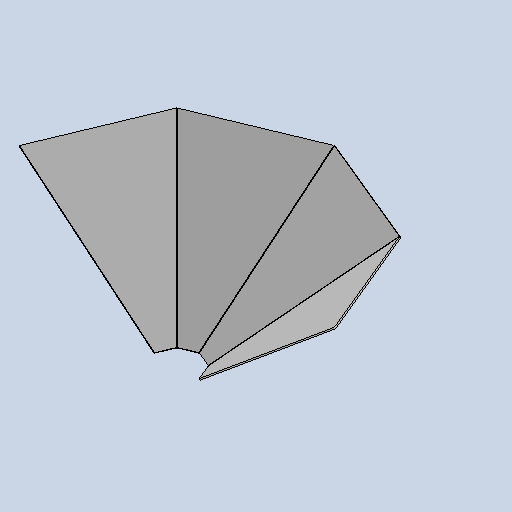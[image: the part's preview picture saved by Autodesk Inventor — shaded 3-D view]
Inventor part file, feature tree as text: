
AUTODESK INVENTOR PART (.ipt)
format: ipt  version: 2025.3 (Build 293356030, 356C)  size: 219,648 bytes
history: native  units: mm
features: sketch x2, plane x1, loft x1, sheet_metal_op x1, other x1
ambient origin geometry x8: Origin, YZ Plane, XZ Plane, XY Plane, X Axis, Y Axis, Z Axis, Center Point
bodies: Body1 (feature_tree)
feature tree (6):
  sketch  "Sketch15"  dims[d117=160.0mm d118=450.0mm]
  plane  "Work Plane1"
  loft  "Lofted Flange1"
  sketch  "Sketch16"  dims[d119=2.0mm d120=0.5mm d121=2.0mm d122=2.0mm d123=1.0mm d124=4.0mm d125=2.0mm d126=59.0mm]
  sheet_metal_op  "Bend1"
  other  "Definition1"
